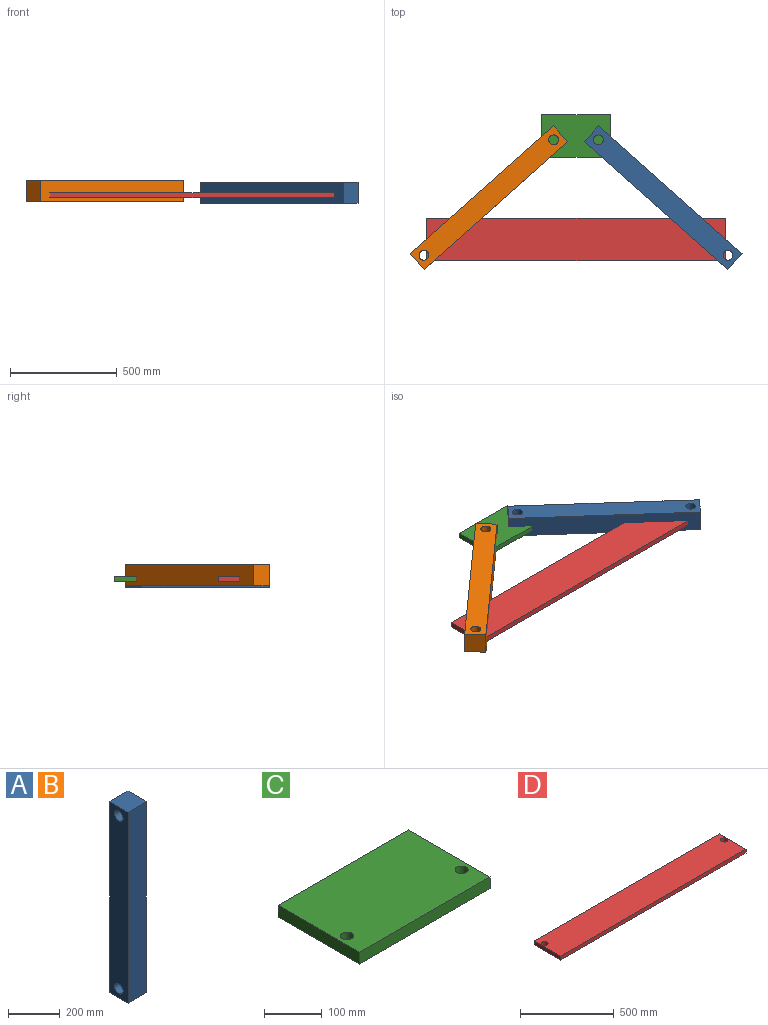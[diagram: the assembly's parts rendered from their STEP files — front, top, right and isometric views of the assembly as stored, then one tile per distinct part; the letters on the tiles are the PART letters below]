
ASSEMBLY  parts=4 mates=5
PART A: 8 faces, bbox 100x100x900 mm
  f0: plane 900x100mm, normal (1,0,0), area 86672.3mm2, adj f2,f3,f4,f5,f6,f7
  f1: plane 900x100mm, normal (-1,0,0), area 86672.3mm2, adj f2,f3,f4,f5,f6,f7
  f2: plane 900x100mm, normal (0,-1,0), area 90000mm2, adj f0,f1,f4,f5
  f3: plane 900x100mm, normal (0,1,0), area 90000mm2, adj f0,f1,f4,f5
  f4: plane 100x100mm, normal (0,0,1), area 10000mm2, adj f0,f1,f2,f3
  f5: plane 100x100mm, normal (0,0,-1), area 10000mm2, adj f0,f1,f2,f3
  f6: cylinder r=23.01mm len=100mm, axis (-1,0,0), area 14459.8mm2, adj f0,f1
  f7: cylinder r=23.01mm len=100mm, axis (-1,0,0), area 14459.8mm2, adj f0,f1
PART B: same geometry as A
PART C: 8 faces, bbox 320x200x25 mm
  f0: plane 320x200mm, normal (0,0,1), area 63195.3mm2, adj f2,f3,f4,f5,f6,f7
  f1: plane 320x200mm, normal (0,0,-1), area 63195.3mm2, adj f2,f3,f4,f5,f6,f7
  f2: plane 320x25mm, normal (0,1,0), area 8000mm2, adj f0,f1,f3,f5
  f3: plane 200x25mm, normal (-1,0,0), area 5000mm2, adj f0,f1,f2,f4
  f4: plane 320x25mm, normal (0,-1,0), area 8000mm2, adj f0,f1,f3,f5
  f5: plane 200x25mm, normal (1,0,0), area 5000mm2, adj f0,f1,f2,f4
  f6: cylinder r=11.32mm len=25mm, axis (0,0,1), area 1777.7mm2, adj f0,f1
  f7: cylinder r=11.32mm len=25mm, axis (0,0,1), area 1777.7mm2, adj f0,f1
PART D: 8 faces, bbox 1400x200x25 mm
  f0: plane 1400x200mm, normal (0,0,1), area 277775.6mm2, adj f2,f3,f4,f5,f6,f7
  f1: plane 1400x200mm, normal (0,0,-1), area 277775.6mm2, adj f2,f3,f4,f5,f6,f7
  f2: plane 1400x25mm, normal (0,1,0), area 35000mm2, adj f0,f1,f3,f5
  f3: plane 200x25mm, normal (-1,0,0), area 5000mm2, adj f0,f1,f2,f4
  f4: plane 1400x25mm, normal (0,-1,0), area 35000mm2, adj f0,f1,f3,f5
  f5: plane 200x25mm, normal (1,0,0), area 5000mm2, adj f0,f1,f2,f4
  f6: cylinder r=18.82mm len=37.63mm, axis (0,0,1), area 2955.5mm2, adj f0,f1
  f7: cylinder r=18.82mm len=37.63mm, axis (0,0,1), area 2955.5mm2, adj f0,f1
PLACE A rot(axis=(-0.34,-0.88,-0.34),97.3deg) t=(125.9,-434.56,23.83)mm
PLACE B rot(axis=(-0.68,-0.26,-0.68),150.9deg) t=(-1364.29,-434.56,31.17)mm
PLACE C t=(-219.66,-56.97,0)mm fixed
PLACE D rot(axis=(0,0,-1),180deg) t=(291.35,139.99,0)mm
MATE cylindrical A.f1 <-> C.f6  axis (0,0,-1) through (-478.7,103.73,-26.17)mm
MATE cylindrical D.f7 <-> A.f0  axis (0,0,-1) through (58.3,-374.38,0)mm
MATE cylindrical B.f0 <-> D.f6  axis (0,0,1) through (-1296.7,-374.38,81.17)mm
MATE cylindrical B.f1 <-> C.f7  axis (0,0,-1) through (-759.7,103.73,-18.83)mm
MATE parallel C.f2 <-> D.f2  axis (0,1,0) through (-619.2,253.73,12.5)mm
